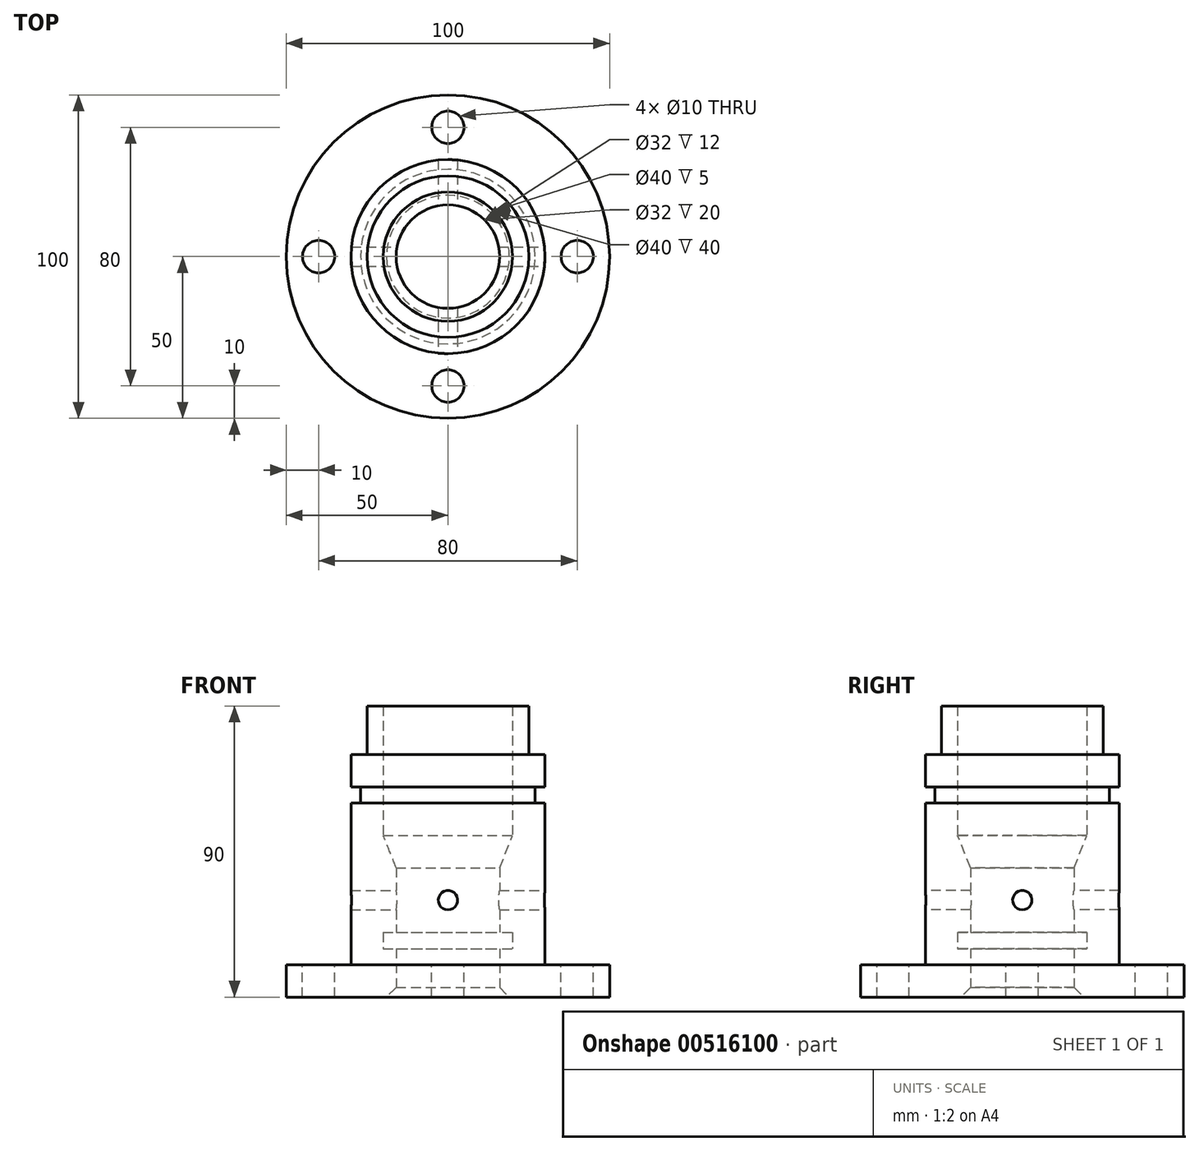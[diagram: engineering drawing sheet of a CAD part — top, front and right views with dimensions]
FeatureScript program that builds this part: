
annotation { "Feature Type Name" : "Feature", "Feature Type Description" : "" }
export const myFeature = defineFeature(function(context is Context, id is Id, definition is map)
    precondition{}
    {
        {
            var Q0;
            Q0=qCreatedBy(makeId("Right.planeOp"),FACE);
            var sketch = newSketch(context, id + "F0", { "sketchPlane" : qUnion([Q0])});
            skLineSegment(sketch, "E0", {"start": v(-16, 0) * mm, "end": v(-16, 15) * mm});
            skLineSegment(sketch, "E1", {"start": v(-16, 15) * mm, "end": v(-20, 15) * mm});
            skLineSegment(sketch, "E2", {"start": v(-20, 15) * mm, "end": v(-20, 20) * mm});
            skLineSegment(sketch, "E3", {"start": v(-20, 20) * mm, "end": v(-16, 20) * mm});
            skLineSegment(sketch, "E4", {"start": v(-16, 20) * mm, "end": v(-16, 40) * mm});
            skLineSegment(sketch, "E5", {"start": v(0, 0) * mm, "end": v(0, 90) * mm, "construction": true});
            skLineSegment(sketch, "E6", {"start": v(-20, 90) * mm, "end": v(-20, 50) * mm});
            skLineSegment(sketch, "E7", {"start": v(-20, 50) * mm, "end": v(-16, 40) * mm});
            skLineSegment(sketch, "E8", {"start": v(-20, 90) * mm, "end": v(-25, 90) * mm});
            skLineSegment(sketch, "E9", {"start": v(-25, 90) * mm, "end": v(-25, 75) * mm});
            skLineSegment(sketch, "E10", {"start": v(-25, 75) * mm, "end": v(-30, 75) * mm});
            skLineSegment(sketch, "E11", {"start": v(-30, 75) * mm, "end": v(-30, 65) * mm});
            skLineSegment(sketch, "E12", {"start": v(-30, 65) * mm, "end": v(-27, 65) * mm});
            skLineSegment(sketch, "E13", {"start": v(-27, 65) * mm, "end": v(-27, 60) * mm});
            skLineSegment(sketch, "E14", {"start": v(-27, 60) * mm, "end": v(-30, 60) * mm});
            skLineSegment(sketch, "E15", {"start": v(-30, 60) * mm, "end": v(-30, 10) * mm});
            skLineSegment(sketch, "E16", {"start": v(-16, 0) * mm, "end": v(-50, 0) * mm});
            skLineSegment(sketch, "E17", {"start": v(-30, 10) * mm, "end": v(-50, 10) * mm});
            skLineSegment(sketch, "E18", {"start": v(-50, 10) * mm, "end": v(-50, 0) * mm});
            skSolve(sketch);
        }
        {
            var Q0;
            Q0=makeQuery(id+"F0.imprint","IMPRINT",FACE,{"disambiguationData":[TD([[makeQuery(id+"F0.imprint","IMPRINT",EDGE,{"derivedFrom":sQuery(id+"F0.wireOp",EDGE,"E0")}),1.0]])]});
            var Q1;
            Q1=sQuery(id+"F0.wireOp",EDGE,"E5");
            revolve(context, id + "F1", {"entities" : qUnion([Q0]), "axis" : qUnion([Q1]), "revolveType" : RevolveType.FULL});
        }
        {
            var Q0;
            Q0=makeQuery(id+"F1.opRevolve","SWEPT_EDGE",EDGE,{"disambiguationData":[OSD([sQuery(id+"F0.wireOp",EDGE,"E0"),sQuery(id+"F0.wireOp",EDGE,"E16")])]});
            chamfer(context, id + "F2", {"entities" : qUnion([Q0]), "width" : 3 * mm, "tangentPropagation" : true});
        }
        {
            var Q0;
            Q0=qCreatedBy(makeId("Front.planeOp"),FACE);
            var sketch = newSketch(context, id + "F3", { "sketchPlane" : qUnion([Q0])});
            skCircle(sketch, "E19", {"center": v(0, 30) * mm, "radius": 3 * mm});
            skSolve(sketch);
        }
        {
            var Q0;
            Q0=makeQuery(id+"F3.imprint","IMPRINT",FACE,{"disambiguationData":[TD([[makeQuery(id+"F3.imprint","IMPRINT",EDGE,{"derivedFrom":sQuery(id+"F3.wireOp",EDGE,"E19")}),1.0]])]});
            var Q1;
            Q1=sQuery(id+"F3.wireOp",EDGE,"E19");
            extrude(context, id + "F4", {"entities" : qUnion([Q0]), "operationType" : NewBodyOperationType.REMOVE, "surfaceEntities" : qUnion([Q1]), "endBound" : BoundingType.SYMMETRIC, "oppositeDirection" : true, "depth" : 100 * mm, "offsetDistance" : 25 * mm});
        }
        {
            var Q0;
            Q0=qCreatedBy(makeId("Right.planeOp"),FACE);
            var sketch = newSketch(context, id + "F5", { "sketchPlane" : qUnion([Q0])});
            skCircle(sketch, "E20", {"center": v(0, 30) * mm, "radius": 3 * mm});
            skSolve(sketch);
        }
        {
            var Q0;
            Q0=makeQuery(id+"F5.imprint","IMPRINT",FACE,{"disambiguationData":[TD([[makeQuery(id+"F5.imprint","IMPRINT",EDGE,{"derivedFrom":sQuery(id+"F5.wireOp",EDGE,"E20")}),1.0]])]});
            extrude(context, id + "F6", {"entities" : qUnion([Q0]), "operationType" : NewBodyOperationType.REMOVE, "endBound" : BoundingType.SYMMETRIC, "oppositeDirection" : true, "depth" : 100 * mm, "offsetDistance" : 25 * mm});
        }
        {
            var Q0;
            Q0=makeQuery(id+"F1.opRevolve","SWEPT_FACE",FACE,{"disambiguationData":[OSD([sQuery(id+"F0.wireOp",EDGE,"E17")])]});
            var sketch = newSketch(context, id + "F7", { "sketchPlane" : qUnion([Q0])});
            skCircle(sketch, "E21", {"center": v(40, 0) * mm, "radius": 5 * mm});
            skCircle(sketch, "E22", {"center": v(0, 40) * mm, "radius": 5 * mm});
            skCircle(sketch, "E23", {"center": v(-40, 0) * mm, "radius": 5 * mm});
            skCircle(sketch, "E24", {"center": v(0, -40) * mm, "radius": 5 * mm});
            skSolve(sketch);
        }
        {
            var Q0;
            Q0=makeQuery(id+"F7.imprint","IMPRINT",FACE,{"disambiguationData":[TD([[makeQuery(id+"F7.imprint","IMPRINT",EDGE,{"derivedFrom":sQuery(id+"F7.wireOp",EDGE,"E24")}),1.0]])]});
            var Q1;
            Q1=makeQuery(id+"F7.imprint","IMPRINT",FACE,{"disambiguationData":[TD([[makeQuery(id+"F7.imprint","IMPRINT",EDGE,{"derivedFrom":sQuery(id+"F7.wireOp",EDGE,"E21")}),1.0]])]});
            var Q2;
            Q2=makeQuery(id+"F7.imprint","IMPRINT",FACE,{"disambiguationData":[TD([[makeQuery(id+"F7.imprint","IMPRINT",EDGE,{"derivedFrom":sQuery(id+"F7.wireOp",EDGE,"E22")}),1.0]])]});
            var Q3;
            Q3=makeQuery(id+"F7.imprint","IMPRINT",FACE,{"disambiguationData":[TD([[makeQuery(id+"F7.imprint","IMPRINT",EDGE,{"derivedFrom":sQuery(id+"F7.wireOp",EDGE,"E23")}),1.0]])]});
            extrude(context, id + "F8", {"entities" : qUnion([Q0, Q1, Q2, Q3]), "operationType" : NewBodyOperationType.REMOVE, "endBound" : BoundingType.UP_TO_NEXT, "oppositeDirection" : true, "depth" : 25 * mm, "offsetDistance" : 25 * mm});
        }
    });
